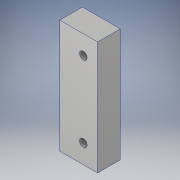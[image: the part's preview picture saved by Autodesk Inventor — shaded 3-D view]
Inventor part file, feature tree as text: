
AUTODESK INVENTOR PART (.ipt)
format: ipt  version: 2018 (Build 220112000, 112)  size: 102,912 bytes
history: native  units: in
note: dims shown in document units (in); Inventor stores cm internally (conversion verified against a paired STEP export)
features: extrude x1, sketch x1
ambient origin geometry x8: Origin, YZ Plane, XZ Plane, XY Plane, X Axis, Y Axis, Z Axis, Center Point
bodies: Solid1 (feature_tree)
feature tree (2):
  extrude  "Extrusion1"  Depth=3.0in
  sketch  "Sketch1"  dims[d0=1.0in d1=3.0in d2=0.25in d3=0.5in d4=0.5in d5=0.2in d6=0.6in d7=0.0in]
